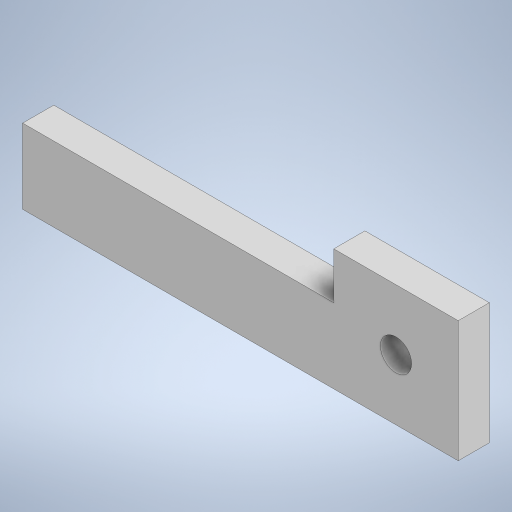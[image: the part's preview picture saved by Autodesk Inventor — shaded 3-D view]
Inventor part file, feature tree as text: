
AUTODESK INVENTOR PART (.ipt)
format: ipt  version: 2023 (Build 270158000, 158)  size: 223,232 bytes
history: native  units: in
note: dims shown in document units (in); Inventor stores cm internally (conversion verified against a paired STEP export)
features: extrude x1, sketch x1
ambient origin geometry x8: Origin, YZ Plane, XZ Plane, XY Plane, X Axis, Y Axis, Z Axis, Center Point
bodies: Body1 (feature_tree)
feature tree (2):
  extrude  "Extrusion2"  Depth=0.4724in
  sketch  "Sketch1"  dims[d0=2.7559in d1=0.4724in d11=0.7874in d12=0.2953in d15=0.3839in d16=0.3937in d17=0.1969in d18=0.1969in d19=0.0in]
